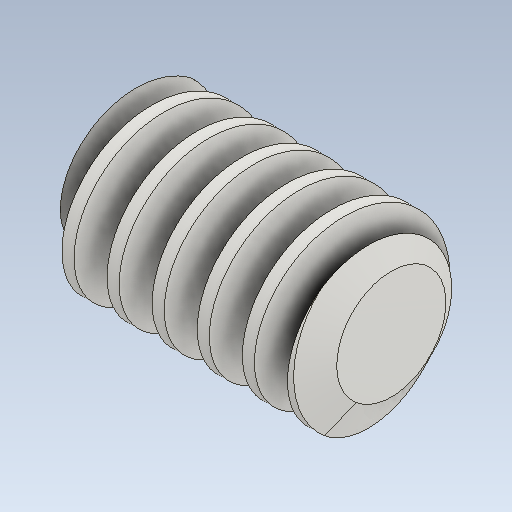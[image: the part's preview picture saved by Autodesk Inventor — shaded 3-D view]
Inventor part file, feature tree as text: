
AUTODESK INVENTOR PART (.ipt)
format: ipt  version: 2021.1 (Build 251245010, 245A)  size: 359,424 bytes
history: native  units: mm (DEFAULTED — no unit token found)
features: other x6, chamfer x2, pattern_circular x2, extrude x1, sketch x1
ambient origin geometry x6: Origin, XZ Plane, X Axis, Y Axis, Z Axis, Center Point
bodies: Solid1 (feature_tree)
feature tree (12):
  extrude  "Base Body"  Depth=10.0mm
  chamfer  "Chamfer1"  Distance=38.1mm
  chamfer  "Chamfer2"  [1 undecoded]
  other  "Tooth Sketch"
  other  "Left Tooth"
  pattern_circular  "Left Tooth Pattern"  [2 undecoded]
  other  "Tooth"
  pattern_circular  "Tooth Pattern"  [2 undecoded]
  other  "Base Body Sketch"
  sketch  "Sketch5"  dims[d4=40.0mm d5=24.255213mm d6=38.1mm d7=0.0mm d8=1.618499mm d9=4.446789mm d10=1.618499mm d11=4.446789mm d12=19.198622mm d14=3.1425mm d24=19.198622mm d25=28.575mm d26=1.5875mm d27=7.680818mm d28=10.106339mm d29=12.248883mm d30=6.35mm d31=10.0mm d32=90.0mm d33=0.0mm d34=90.0deg d35=90.0deg d36=0.0mm d37=0.0mm d43=10.0mm d45=360.0deg d46=45.0deg d47=45.0deg d49=0.0mm d53=0.0mm d54=70.744372mm d55=0.0mm d56=0.0mm d57=20.212678mm d58=25.4mm d59=0.0mm d60=6.35mm d61=25.4mm d62=90.0mm d63=0.0mm d64=90.0deg d65=90.0deg d66=0.0mm d67=0.0mm d68=10.0mm d69=10.0mm d70=360.0deg d72=10.0mm d74=10.0mm d75=10.0mm d76=0.0mm d77=70.744372mm]
  other  "Srf1"
  other  "Pitch Diameter"
note: 5 required parameter values undecoded (feature->parameter linkage not recoverable at this tier; creation-order binding heuristic only, values carry confidence <= 0.55)
